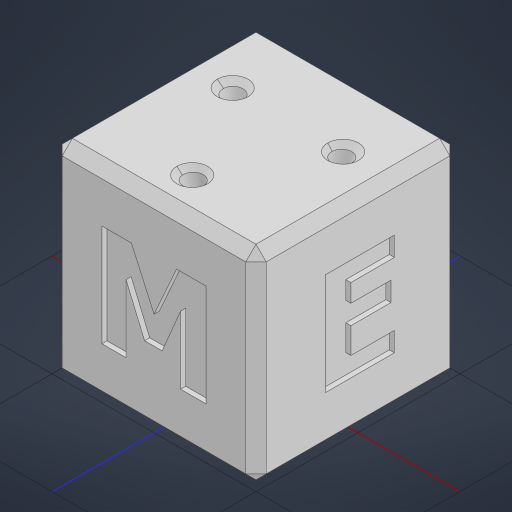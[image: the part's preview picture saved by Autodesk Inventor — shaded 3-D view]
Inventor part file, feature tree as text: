
AUTODESK INVENTOR PART (.ipt)
format: ipt  version: 2023.2 (Build 272271030, 271C)  size: 297,472 bytes
history: native  units: mm
features: sketch x7, other x4, loft x3, chamfer x2, extrude x1, plane x1
ambient origin geometry x8: Origin, YZ Plane, XZ Plane, XY Plane, X Axis, Y Axis, Z Axis, Center Point
bodies: Volumenkörper1 (feature_tree)
feature tree (18):
  extrude  "Extrusion1"  Depth=40.0mm
  plane  "Arbeitsebene2"
  sketch  "Skizze8"  dims[d32=25.0mm]
  sketch  "Skizze9"  dims[d33=4.0mm d34=30.0mm d36=360.0deg d38=15.0mm d39=2.0mm d40=30.0mm d42=360.0deg d44=0.0mm d45=90.0deg d46=0.0mm d47=90.0deg d48=0.0mm d49=90.0deg d50=0.0mm d51=90.0deg d52=0.0mm d53=90.0deg d54=0.0mm d55=90.0deg d56=1.0mm d57=2.0mm d58=45.0deg]
  loft  "Erhebung1"
  loft  "Erhebung2"
  loft  "Erhebung3"
  chamfer  "Fase1"  Distance=30.0mm Angle=360.0deg
  chamfer  "Fase2"  Distance=15.0mm
  sketch  "Skizze4"  dims[d3=0.0mm d18=2.0mm d19=2.0mm d20=45.0deg]
  sketch  "Skizze5"  dims[d23=1.0mm d24=0.0mm d25=1.0mm d26=0.0mm]
  sketch  "Skizze6"  dims[d27=1.0mm d28=0.0mm d29=1.0mm d30=0.0mm]
  sketch  "Skizze7"  dims[d31=-27.0mm]
  other  "Prägen1"
  other  "Prägen2"
  other  "Prägen3"
  other  "Prägen4"
  sketch  "Skizze1"  dims[d0=40.0mm d2=40.0mm]
